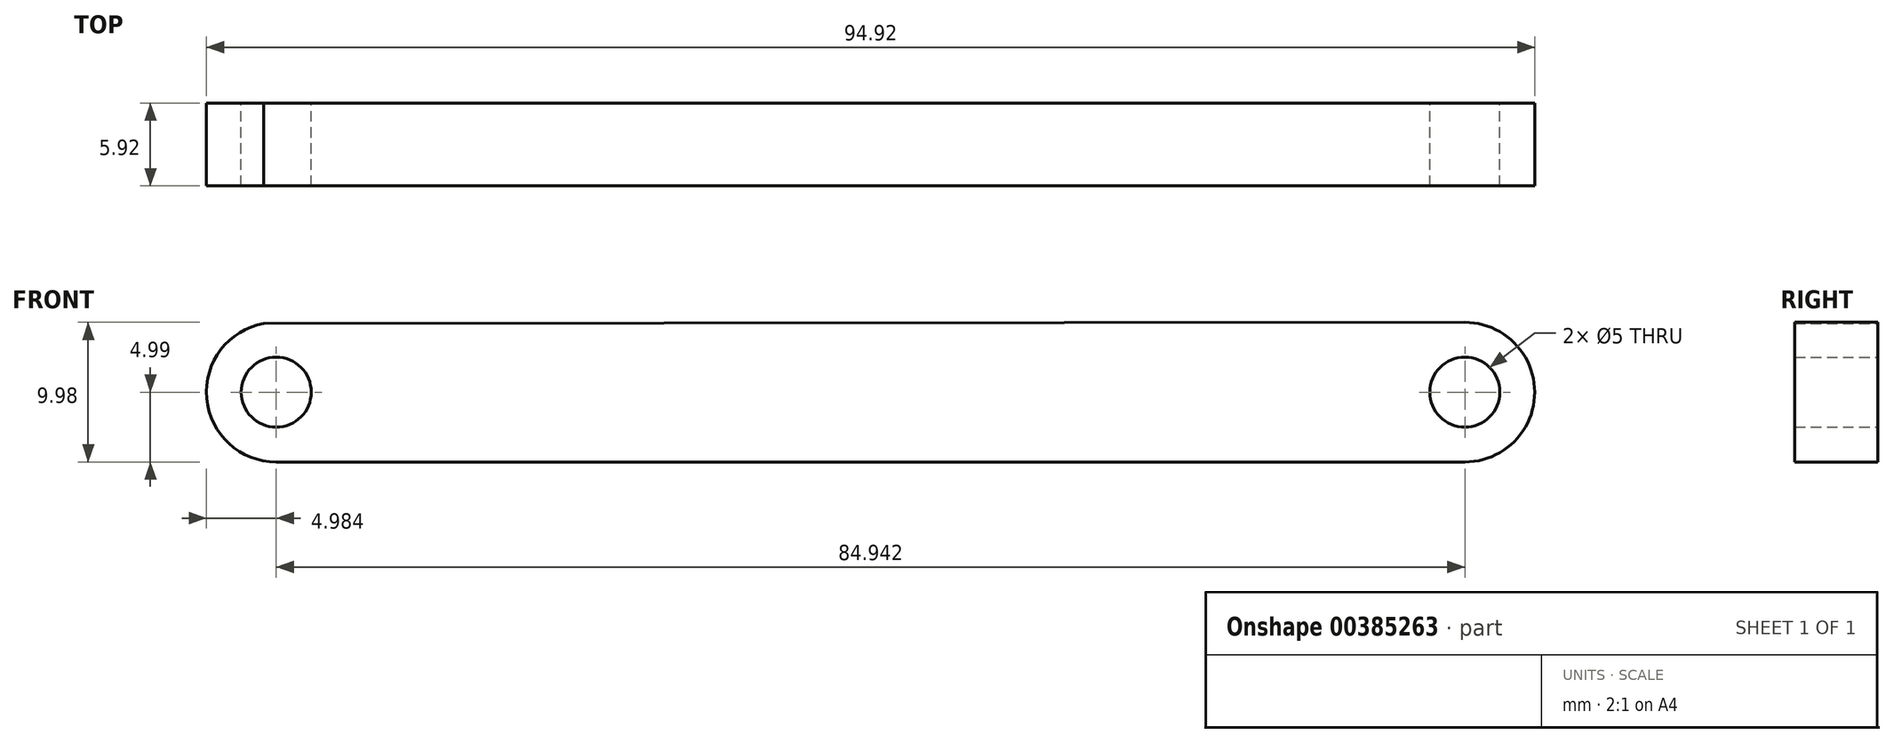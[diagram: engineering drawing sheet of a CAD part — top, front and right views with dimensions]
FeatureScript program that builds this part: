
annotation { "Feature Type Name" : "Feature", "Feature Type Description" : "" }
export const myFeature = defineFeature(function(context is Context, id is Id, definition is map)
    precondition{}
    {
        {
            var Q0;
            Q0=qCreatedBy(makeId("Front.planeOp"),FACE);
            var sketch = newSketch(context, id + "F0", { "sketchPlane" : qUnion([Q0])});
            skArc(sketch, "E0", {"start": v(-47.57, 4.9) * mm, "mid": v(-51.65, -0.44) * mm, "end": v(-46.69, -4.99) * mm});
            skArc(sketch, "E1", {"start": v(38.26, -4.99) * mm, "mid": v(43.25, 0) * mm, "end": v(38.25, 4.99) * mm});
            skLineSegment(sketch, "E2", {"start": v(-47.57, 4.9) * mm, "end": v(38.25, 4.99) * mm});
            skLineSegment(sketch, "E3", {"start": v(-46.69, -4.99) * mm, "end": v(38.26, -4.99) * mm});
            skCircle(sketch, "E4", {"center": v(-46.69, 0) * mm, "radius": 2.5 * mm});
            skCircle(sketch, "E5", {"center": v(38.26, 0) * mm, "radius": 2.5 * mm});
            skSolve(sketch);
        }
        {
            var Q0;
            Q0 = qSketchRegion(id + "F0", true);
            extrude(context, id + "F1", {"entities" : qUnion([Q0]), "depth" : 5.92 * mm});
        }
    });
